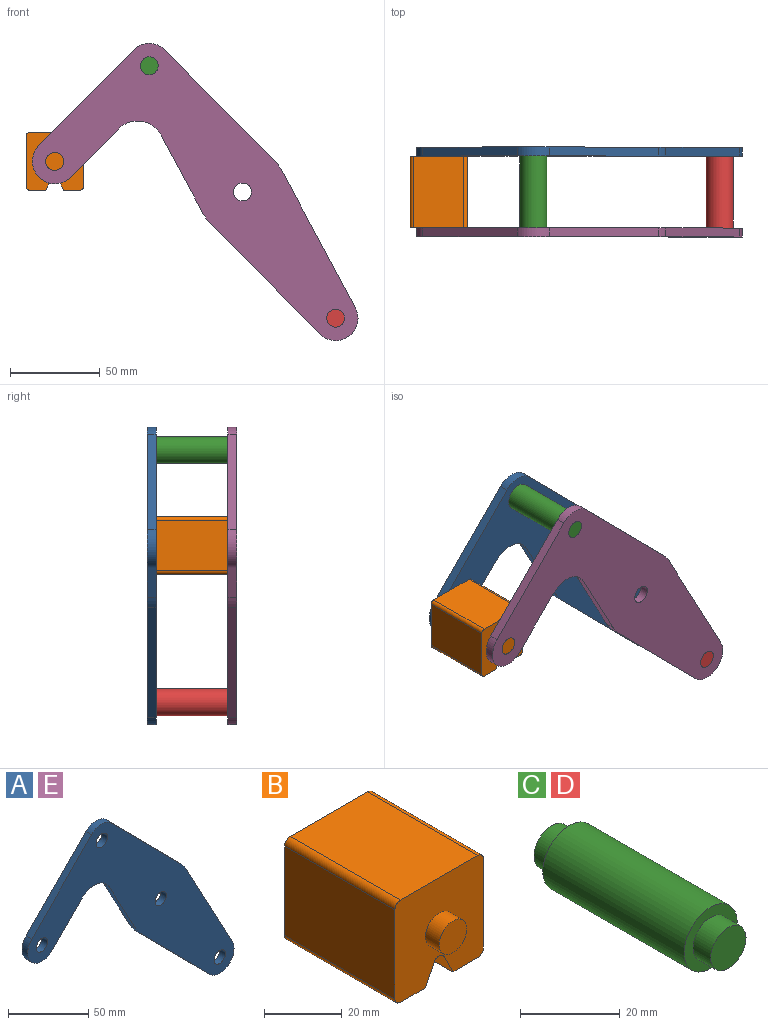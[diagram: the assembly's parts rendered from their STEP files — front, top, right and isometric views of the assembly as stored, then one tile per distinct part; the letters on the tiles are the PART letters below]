
ASSEMBLY  parts=5 mates=3
PART A: 18 faces, bbox 181.7x5x165.8 mm
  f0: plane 43.49x23.35mm, normal (-0.88,0,-0.47), area 246.8mm2, adj f1,f14,f16,f17
  f1: cylinder r=25mm len=5.75mm, axis (0,1,0), area 35.8mm2, adj f0,f2,f16,f17
  f2: plane 61.6x60.87mm, normal (-0.71,0,-0.7), area 433mm2, adj f1,f3,f16,f17
  f3: cylinder r=12.5mm len=21.39mm, axis (0,1,0), area 178.4mm2, adj f2,f4,f16,f17
  f4: plane 76.3x40.96mm, normal (0.88,0,0.47), area 433mm2, adj f3,f5,f16,f17
  f5: cylinder r=25mm len=5.75mm, axis (0,1,0), area 35.8mm2, adj f4,f6,f16,f17
  f6: plane 61.6x60.87mm, normal (0.71,0,0.7), area 433mm2, adj f5,f7,f16,f17
  f7: cylinder r=12.5mm len=17.78mm, axis (0,1,0), area 98.9mm2, adj f6,f8,f16,f17
  f8: plane 53.35x52.71mm, normal (-0.71,0,0.7), area 375mm2, adj f7,f9,f16,f17
  f9: cylinder r=12.5mm len=21.39mm, axis (0,1,0), area 196.3mm2, adj f8,f10,f16,f17
  f10: plane 26.86x26.54mm, normal (0.71,0,-0.7), area 188.8mm2, adj f9,f14,f16,f17
  f11: cylinder r=5mm len=10mm, axis (0,1,0), area 157.1mm2, adj f16,f17
  f12: cylinder r=5mm len=10mm, axis (0,1,0), area 157.1mm2, adj f16,f17
  f13: cylinder r=5mm len=10mm, axis (0,1,0), area 157.1mm2, adj f16,f17
  f14: cylinder r=15mm len=23.89mm, axis (0,1,0), area 140.2mm2, adj f0,f10,f16,f17
  f15: cylinder r=5mm len=10mm, axis (0,1,0), area 157.1mm2, adj f16,f17
  f16: plane 181.66x165.78mm, normal (0,-1,0), area 8710.1mm2, adj f0,f1,f2,f3,f4,f5,f6,f7
  f17: plane 181.66x165.78mm, normal (0,1,0), area 8710.1mm2, adj f0,f1,f2,f3,f4,f5,f6,f7
PART B: 18 faces, bbox 32.1x50x32.1 mm
  f0: plane 40x28.08mm, normal (1,0,0), area 1123.1mm2, adj f4,f10,f13,f14
  f1: plane 40x9.04mm, normal (0,0,-1), area 361.6mm2, adj f2,f4,f10,f14
  f2: plane 40x6.42mm, normal (-0.89,0,-0.45), area 287.2mm2, adj f1,f4,f10,f15
  f3: plane 40x6.42mm, normal (0.89,0,-0.45), area 287.2mm2, adj f4,f5,f10,f15
  f4: plane 32.08x32.08mm, normal (0,-1,0), area 900.6mm2, adj f0,f1,f2,f3,f5,f6,f7,f9
  f5: plane 40x9.04mm, normal (0,0,-1), area 361.6mm2, adj f3,f4,f10,f16
  f6: plane 40x28.08mm, normal (0,0,1), area 1123.1mm2, adj f4,f10,f13,f17
  f7: plane 40x28.08mm, normal (-1,0,0), area 1123.1mm2, adj f4,f10,f16,f17
  f8: plane 10x10mm, normal (0,-1,0), area 78.5mm2, adj f9
  f9: cylinder r=5mm len=10mm, axis (0,1,0), area 157.1mm2, adj f4,f8
  f10: plane 32.08x32.08mm, normal (0,1,0), area 900.6mm2, adj f0,f1,f2,f3,f5,f6,f7,f12
  f11: plane 10x10mm, normal (0,1,0), area 78.5mm2, adj f12
  f12: cylinder r=5mm len=10mm, axis (0,-1,0), area 157.1mm2, adj f10,f11
  f13: cylinder r=2mm len=40mm, axis (0,1,0), area 125.7mm2, adj f0,f4,f6,f10
  f14: cylinder r=2mm len=40mm, axis (0,-1,0), area 125.7mm2, adj f0,f1,f4,f10
  f15: cylinder r=2mm len=40mm, axis (0,1,0), area 177.1mm2, adj f2,f3,f4,f10
  f16: cylinder r=2mm len=40mm, axis (0,1,0), area 125.7mm2, adj f4,f5,f7,f10
  f17: cylinder r=2mm len=40mm, axis (0,-1,0), area 125.7mm2, adj f4,f6,f7,f10
PART C: 7 faces, bbox 15x50x15 mm
  f0: cylinder r=7.5mm len=40mm, axis (0,-1,0), area 1885mm2, adj f2,f5
  f1: cylinder r=5mm len=10mm, axis (0,1,0), area 157.1mm2, adj f2,f3
  f2: plane 15x15mm, normal (0,-1,0), area 98.2mm2, adj f0,f1
  f3: plane 10x10mm, normal (0,-1,0), area 78.5mm2, adj f1
  f4: cylinder r=5mm len=10mm, axis (0,-1,0), area 157.1mm2, adj f5,f6
  f5: plane 15x15mm, normal (0,1,0), area 98.2mm2, adj f0,f4
  f6: plane 10x10mm, normal (0,1,0), area 78.5mm2, adj f4
PART D: same geometry as C
PART E: same geometry as A
PLACE A t=(-7.26,24.69,-1.92)mm
PLACE B t=(-7.26,-20.31,-1.92)mm
PLACE C t=(-7.26,-20.31,-1.92)mm
PLACE D t=(96.69,-20.31,-142.7)mm
PLACE E t=(-7.26,-20.31,-1.92)mm fixed
MATE revolute B.f9 <-> E.f9  axis (0,1,0) through (-111.95,-20.31,15.12)mm
MATE fastened C.f0 <-> A.f7  axis (0,1,0) through (-59.23,19.69,68.47)mm
MATE fastened E.f3 <-> D.f0  axis (0,1,0) through (44.72,-20.31,-72.31)mm
